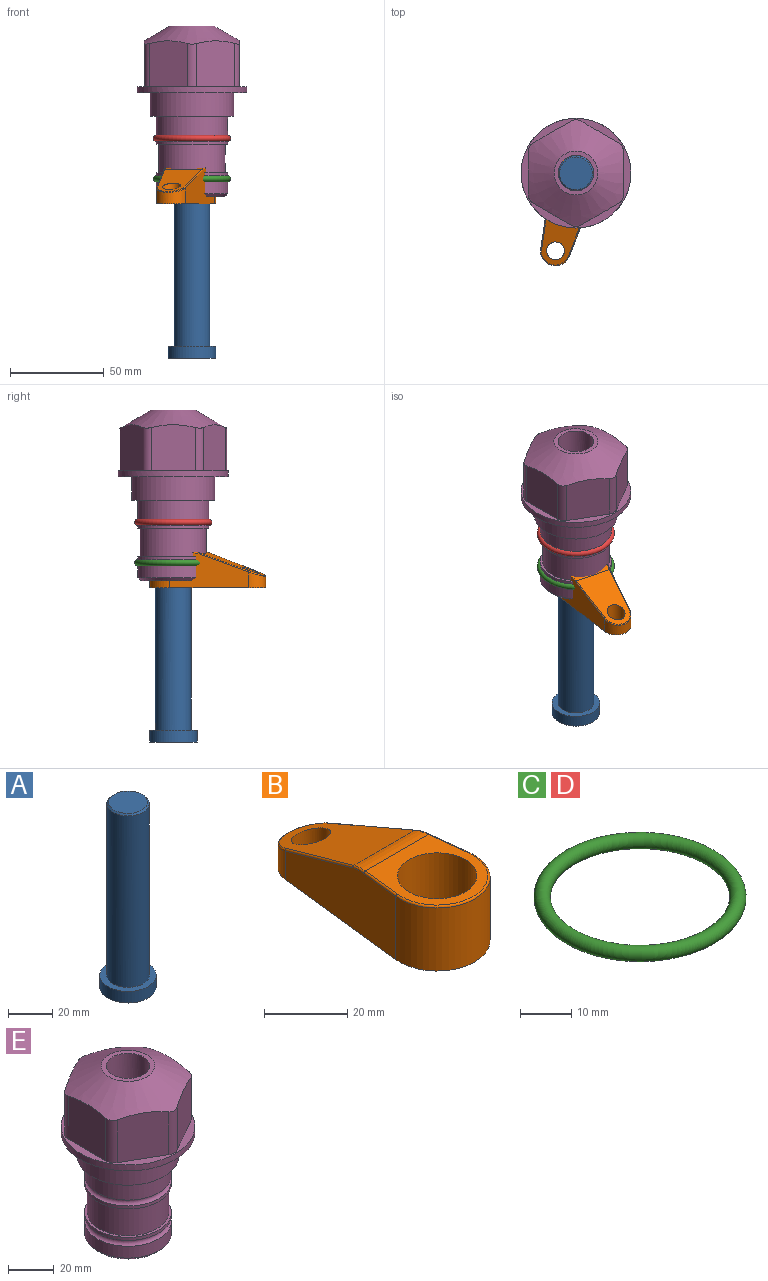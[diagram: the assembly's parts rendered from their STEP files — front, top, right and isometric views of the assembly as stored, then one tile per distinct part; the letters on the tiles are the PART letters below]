
ASSEMBLY  parts=5 mates=3
PART A: 6 faces, bbox 25.4x25.4x101.6 mm
  f0: plane 17.46x17.46mm, normal (0,0,1), area 239.5mm2, adj f5
  f1: plane 25.4x25.4mm, normal (0,0,-1), area 506.7mm2, adj f2
  f2: cylinder r=12.7mm len=25.4mm, axis (0,0,1), area 506.7mm2, adj f1,f3
  f3: plane 25.4x25.4mm, normal (0,0,1), area 221.7mm2, adj f2,f4
  f4: cylinder r=9.53mm len=94.46mm, axis (0,0,1), area 5653mm2, adj f3,f5
  f5: cone r=8.73mm half-angle=45deg, axis (0,0,-1), area 64.4mm2, adj f0,f4
PART B: 44 faces, bbox 27.5x64.5x19.1 mm
  f0: plane 2.3x0.95mm, normal (0,0,-1), area 1mm2, adj f25,f30,f34
  f1: plane 63.5x25.4mm, normal (0,0,-1), area 561.7mm2, adj f2,f3,f4,f5,f6,f7,f19,f20
  f2: cylinder r=12.7mm len=25.4mm, axis (0,0,-1), area 792.2mm2, adj f1,f3,f5,f13
  f3: plane 42.33x18.54mm, normal (0.99,0.11,0), area 647mm2, adj f1,f2,f4,f11,f12,f14
  f4: cylinder r=7.94mm len=15.78mm, axis (0,0,-1), area 158.6mm2, adj f1,f3,f5,f16
  f5: plane 42.33x18.54mm, normal (-0.99,0.11,0), area 647mm2, adj f1,f2,f4,f15,f17,f18
  f6: cylinder r=9.53mm len=19.05mm, axis (0,0,-1), area 1140.1mm2, adj f1,f8
  f7: cylinder r=4.76mm len=10.98mm, axis (0,0,-1), area 276.1mm2, adj f1,f9
  f8: plane 25.83x24.38mm, normal (0,0,1), area 262.2mm2, adj f6,f10,f11,f13,f15
  f9: plane 32.49x20.55mm, normal (0,0.34,0.94), area 489.9mm2, adj f7,f10,f14,f16,f18
  f10: cylinder r=12.7mm len=21.49mm, axis (-1,0,0), area 93.2mm2, adj f8,f9,f12,f17
  f11: cylinder r=0.51mm len=12.34mm, axis (0.11,-0.99,0), area 9.9mm2, adj f3,f8,f12,f13
  f12: bspline ~7.62x1.64mm, area 3.5mm2, adj f3,f10,f11,f14
  f13: torus R=12.19mm, axis (0,0,1), area 33.6mm2, adj f2,f8,f11,f15
  f14: cylinder r=0.51mm len=26.01mm, axis (0.1,-0.93,0.34), area 21.6mm2, adj f3,f9,f12,f16
  f15: cylinder r=0.51mm len=12.34mm, axis (0.11,0.99,0), area 9.9mm2, adj f5,f8,f13,f17
  f16: bspline ~15.78x7.05mm, area 15.7mm2, adj f4,f9,f14,f18
  f17: bspline ~7.62x1.64mm, area 3.5mm2, adj f5,f10,f15,f18
  f18: cylinder r=0.51mm len=26.01mm, axis (0.1,0.93,-0.34), area 21.6mm2, adj f5,f9,f16,f17
  f19: plane 21.6x14.29mm, normal (-0.99,-0.11,0), area 242.6mm2, adj f1,f26,f28,f34,f36,f38
  f20: plane 21.6x14.29mm, normal (0.99,-0.11,0), area 242.6mm2, adj f1,f27,f29,f37,f39,f41
  f21: cylinder r=12.7mm len=14.29mm, axis (0,0,-1), area 173.2mm2, adj f1,f26,f27,f30,f31,f33
  f22: cylinder r=7.94mm len=7.63mm, axis (0,0,-1), area 53.8mm2, adj f1,f28,f29,f42
  f23: plane 2.3x0.95mm, normal (0,0,-1), area 1mm2, adj f25,f33,f37
  f24: plane 17.94x12.32mm, normal (0,-0.34,-0.94), area 191.2mm2, adj f25,f38,f41,f42
  f25: cylinder r=9.53mm len=12.93mm, axis (-1,0,0), area 37.5mm2, adj f0,f23,f24,f31,f36,f39
  f26: cylinder r=1.59mm len=14.29mm, axis (0,0,-1), area 49mm2, adj f1,f19,f21,f32
  f27: cylinder r=1.59mm len=14.29mm, axis (0,0,-1), area 49mm2, adj f1,f20,f21,f35
  f28: cylinder r=1.59mm len=7.28mm, axis (0,0,-1), area 22.1mm2, adj f1,f19,f22,f40
  f29: cylinder r=1.59mm len=7.28mm, axis (0,0,-1), area 22.1mm2, adj f1,f20,f22,f43
  f30: torus R=14.29mm, axis (0,0,1), area 5.8mm2, adj f0,f21,f31,f32
  f31: bspline ~11.06x2.73mm, area 20.8mm2, adj f21,f25,f30,f33
  f32: sphere r=1.59mm, area 5.4mm2, adj f26,f30,f34
  f33: torus R=14.29mm, axis (0,0,1), area 5.8mm2, adj f21,f23,f31,f35
  f34: cylinder r=1.59mm len=1.68mm, axis (-0.11,0.99,0), area 2.4mm2, adj f0,f19,f32,f36
  f35: sphere r=1.59mm, area 5.4mm2, adj f27,f33,f37
  f36: bspline ~5.82x2.33mm, area 7.7mm2, adj f19,f25,f34,f38
  f37: cylinder r=1.59mm len=1.68mm, axis (0.11,0.99,0), area 2.4mm2, adj f20,f23,f35,f39
  f38: cylinder r=1.59mm len=18.33mm, axis (0.1,-0.93,0.34), area 46.7mm2, adj f19,f24,f36,f40
  f39: bspline ~5.82x2.33mm, area 7.7mm2, adj f20,f25,f37,f41
  f40: sphere r=1.59mm, area 3.6mm2, adj f28,f38,f42
  f41: cylinder r=1.59mm len=18.33mm, axis (0.1,0.93,-0.34), area 46.7mm2, adj f20,f24,f39,f43
  f42: bspline ~8.31x1.84mm, area 15.3mm2, adj f22,f24,f40,f43
  f43: sphere r=1.59mm, area 3.6mm2, adj f29,f41,f42
PART C: 1 faces, bbox 44.7x44.7x3.2 mm
  f0: torus R=19.05mm, axis (0,0,1), area 1193.9mm2
PART D: same geometry as C
PART E: 36 faces, bbox 58.7x58.7x91.2 mm
  f0: cylinder r=17.78mm len=35.56mm, axis (0,0,1), area 1670.8mm2, adj f23,f24,f31
  f1: cylinder r=19.05mm len=38.1mm, axis (0,0,1), area 1191.9mm2, adj f26,f27,f30
  f2: plane 58.66x58.66mm, normal (0,0,-1), area 1150.6mm2, adj f3,f28
  f3: cylinder r=29.33mm len=58.66mm, axis (0,0,-1), area 585.1mm2, adj f2,f4
  f4: plane 58.66x58.66mm, normal (0,0,1), area 475.9mm2, adj f3,f5,f6,f7,f8,f9,f10,f11
  f5: plane 24.5x20.32mm, normal (-0.5,0.87,0), area 562.8mm2, adj f4,f15,f16,f17
  f6: plane 24.5x20.32mm, normal (0.5,0.87,0), area 562.8mm2, adj f4,f14,f15,f17
  f7: plane 24.5x23.48mm, normal (1,0,0), area 562.8mm2, adj f4,f13,f14,f17
  f8: plane 24.5x20.32mm, normal (0.5,-0.87,0), area 562.8mm2, adj f4,f12,f13,f17
  f9: plane 24.5x20.32mm, normal (-0.5,-0.87,0), area 562.8mm2, adj f4,f11,f12,f17
  f10: plane 24.5x23.48mm, normal (-1,0,0), area 562.8mm2, adj f4,f11,f16,f17
  f11: cylinder r=5.08mm len=23.01mm, axis (0,0,-1), area 121.2mm2, adj f4,f9,f10,f17
  f12: cylinder r=5.08mm len=23.01mm, axis (0,0,-1), area 121.2mm2, adj f4,f8,f9,f17
  f13: cylinder r=5.08mm len=23.01mm, axis (0,0,-1), area 121.2mm2, adj f4,f7,f8,f17
  f14: cylinder r=5.08mm len=23.01mm, axis (0,0,-1), area 121.2mm2, adj f4,f6,f7,f17
  f15: cylinder r=5.08mm len=23.01mm, axis (0,0,-1), area 121.2mm2, adj f4,f5,f6,f17
  f16: cylinder r=5.08mm len=23.01mm, axis (0,0,-1), area 121.2mm2, adj f4,f5,f10,f17
  f17: cone r=11.73mm half-angle=60deg, axis (0,0,-1), area 2071.8mm2, adj f5,f6,f7,f8,f9,f10,f11,f12
  f18: plane 23.46x23.46mm, normal (0,0,1), area 147.4mm2, adj f17,f35
  f19: plane 34.93x34.93mm, normal (0,0,-1), area 958mm2, adj f29
  f20: cylinder r=19.05mm len=38.1mm, axis (0,0,1), area 760.1mm2, adj f21,f29
  f21: torus R=19.05mm, axis (0,0,1), area 565.3mm2, adj f20,f22
  f22: cylinder r=19.05mm len=38.1mm, axis (0,0,1), area 190mm2, adj f21,f23
  f23: plane 38.1x38.1mm, normal (0,0,1), area 146.9mm2, adj f0,f22
  f24: plane 38.1x38.1mm, normal (0,0,-1), area 146.9mm2, adj f0,f25
  f25: cylinder r=19.05mm len=38.1mm, axis (0,0,1), area 190mm2, adj f24,f26
  f26: torus R=19.05mm, axis (0,0,1), area 565.3mm2, adj f1,f25
  f27: plane 44.45x44.45mm, normal (0,0,-1), area 411.7mm2, adj f1,f28
  f28: cylinder r=22.23mm len=44.45mm, axis (0,0,1), area 1773.5mm2, adj f2,f27
  f29: cone r=19.05mm half-angle=45deg, axis (0,0,1), area 257.5mm2, adj f19,f20
  f30: cylinder r=3.17mm len=6.75mm, axis (-1,0,0), area 128mm2, adj f1,f33
  f31: cylinder r=3.17mm len=6.35mm, axis (-1,0,0), area 102.5mm2, adj f0,f33
  f32: plane 25.4x25.4mm, normal (0,0,1), area 506.7mm2, adj f33
  f33: cylinder r=12.7mm len=66.42mm, axis (0,0,-1), area 5236.2mm2, adj f30,f31,f32,f34
  f34: cone r=9.53mm half-angle=30deg, axis (0,0,-1), area 443.4mm2, adj f33,f35
  f35: cylinder r=9.53mm len=19.05mm, axis (0,0,-1), area 849mm2, adj f18,f34
PLACE A rot(axis=(0,0,-1),104.8deg) t=(0,0,-113.99)mm
PLACE B rot(axis=(0,0,1),165.2deg) t=(0,0,-59.38)mm
PLACE C t=(0,0,-21.59)mm
PLACE D at identity
PLACE E at identity fixed
MATE fastened C.f0 <-> E.f0  axis (0,0,1) through (0,0,-46.1)mm
MATE cylindrical A.f2 <-> E.f0  axis (0,0,1) through (0,0,-88.35)mm
MATE fastened B.f2 <-> A.f2  axis (0,0,1) through (0,0,-40.33)mm
